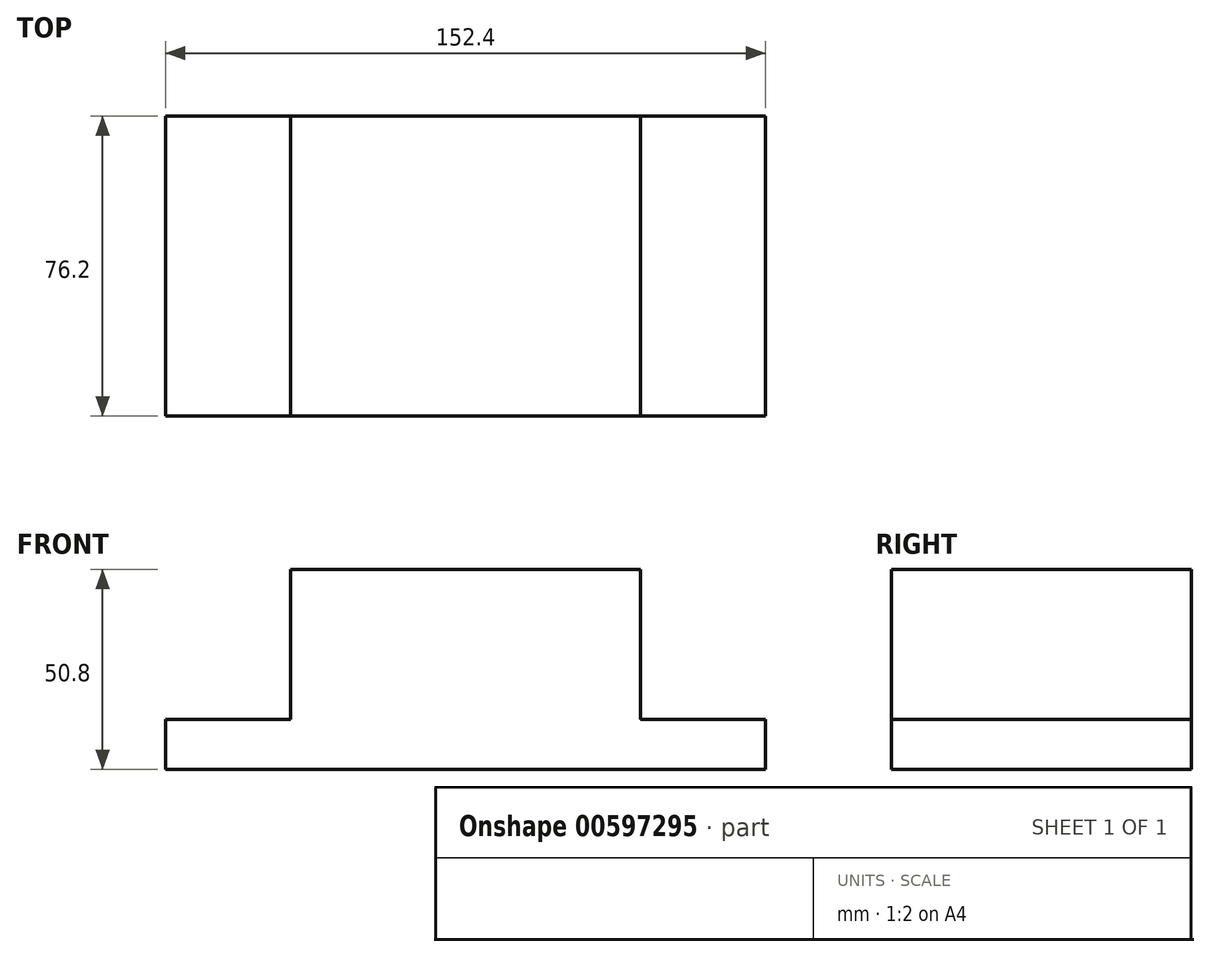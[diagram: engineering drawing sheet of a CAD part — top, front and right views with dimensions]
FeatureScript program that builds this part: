
annotation { "Feature Type Name" : "Feature", "Feature Type Description" : "" }
export const myFeature = defineFeature(function(context is Context, id is Id, definition is map)
    precondition{}
    {
        {
            var Q0;
            Q0=qCreatedBy(makeId("Front.planeOp"),FACE);
            var sketch = newSketch(context, id + "F0", { "sketchPlane" : qUnion([Q0])});
            skLineSegment(sketch, "E0.bottom", {"start": v(0, 0) * mm, "end": v(152.4, 0) * mm});
            skLineSegment(sketch, "E0.top", {"start": v(0, 50.8) * mm, "end": v(152.4, 50.8) * mm});
            skLineSegment(sketch, "E0.left", {"start": v(0, 0) * mm, "end": v(0, 50.8) * mm});
            skLineSegment(sketch, "E0.right", {"start": v(152.4, 0) * mm, "end": v(152.4, 50.8) * mm});
            skSolve(sketch);
        }
        {
            var Q0;
            Q0 = qSketchRegion(id + "F0", true);
            extrude(context, id + "F1", {"entities" : qUnion([Q0]), "oppositeDirection" : true, "depth" : 76.2 * mm, "offsetDistance" : 25.4 * mm});
        }
        {
            var Q0;
            Q0=makeQuery(id+"F1.opExtrude","CAP_FACE",FACE,{"disambiguationData":[OSD([sQuery(id+"F0.wireOp",EDGE,"E0.bottom"),sQuery(id+"F0.wireOp",EDGE,"E0.top"),sQuery(id+"F0.wireOp",EDGE,"E0.left"),sQuery(id+"F0.wireOp",EDGE,"E0.right")])],"isStart":true});
            var sketch = newSketch(context, id + "F2", { "sketchPlane" : qUnion([Q0])});
            skLineSegment(sketch, "E1", {"start": v(0, 0) * mm, "end": v(0, 12.7) * mm});
            skLineSegment(sketch, "E2", {"start": v(0, 12.7) * mm, "end": v(31.75, 12.7) * mm});
            skLineSegment(sketch, "E3", {"start": v(31.75, 12.7) * mm, "end": v(31.75, 50.8) * mm});
            skLineSegment(sketch, "E4", {"start": v(152.4, 0) * mm, "end": v(152.4, 12.7) * mm});
            skLineSegment(sketch, "E5", {"start": v(152.4, 12.7) * mm, "end": v(120.65, 12.7) * mm});
            skLineSegment(sketch, "E6", {"start": v(120.65, 12.7) * mm, "end": v(120.65, 50.8) * mm});
            skLineSegment(sketch, "E7", {"start": v(31.75, 50.8) * mm, "end": v(44.45, 50.8) * mm});
            skLineSegment(sketch, "E8", {"start": v(31.75, 12.7) * mm, "end": v(120.65, 12.7) * mm});
            skLineSegment(sketch, "E9", {"start": v(120.65, 50.8) * mm, "end": v(107.95, 50.8) * mm});
            skLineSegment(sketch, "E10", {"start": v(31.75, 12.7) * mm, "end": v(69.85, 12.7) * mm});
            skLineSegment(sketch, "E11", {"start": v(120.65, 12.7) * mm, "end": v(82.55, 12.7) * mm});
            skLineSegment(sketch, "E12", {"start": v(69.85, 12.7) * mm, "end": v(82.55, 12.7) * mm});
            skLineSegment(sketch, "E13", {"start": v(69.85, 12.7) * mm, "end": v(69.85, 25.4) * mm});
            skLineSegment(sketch, "E14", {"start": v(69.85, 25.4) * mm, "end": v(44.45, 50.8) * mm});
            skLineSegment(sketch, "E15", {"start": v(82.55, 12.7) * mm, "end": v(82.55, 25.4) * mm});
            skLineSegment(sketch, "E16", {"start": v(82.55, 25.4) * mm, "end": v(107.95, 50.8) * mm});
            skSolve(sketch);
        }
        {
            var Q0;
            {var subQ0=sQuery(id+"F2.wireOp",EDGE,"E2");Q0=makeQuery(id+"F2.imprint","IMPRINT",FACE,{"disambiguationData":[TD([[makeQuery(id+"F2.imprint","IMPRINT",EDGE,{"derivedFrom":subQ0}),1.0]])]});}
            var Q1;
            Q1=makeQuery(id+"F2.imprint","IMPRINT",FACE,{"disambiguationData":[TD([[makeQuery(id+"F2.imprint","IMPRINT",EDGE,{"derivedFrom":sQuery(id+"F2.wireOp",EDGE,"E12")}),1.0]])]});
            var Q2;
            {var subQ0=sQuery(id+"F2.wireOp",EDGE,"E5");Q2=makeQuery(id+"F2.imprint","IMPRINT",FACE,{"disambiguationData":[TD([[makeQuery(id+"F2.imprint","IMPRINT",EDGE,{"derivedFrom":subQ0}),-1.0]])]});}
            extrude(context, id + "F3", {"entities" : qUnion([Q0, Q1, Q2]), "operationType" : NewBodyOperationType.REMOVE, "oppositeDirection" : true, "depth" : 76.2 * mm, "offsetDistance" : 25.4 * mm});
        }
    });
